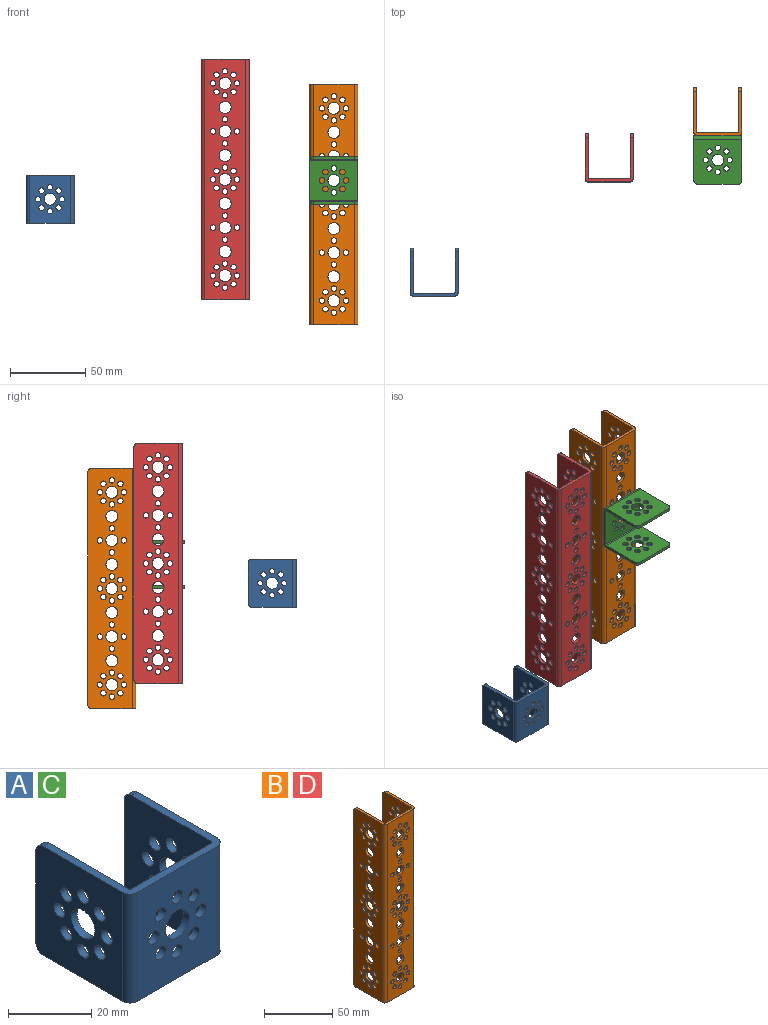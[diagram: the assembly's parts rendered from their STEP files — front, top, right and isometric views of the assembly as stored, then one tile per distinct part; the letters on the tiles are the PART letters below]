
ASSEMBLY  parts=4 mates=1
PART A: 45 faces, bbox 32x32x32 mm
  f0: cylinder r=2.5mm len=32mm, axis (0,0,-1), area 125.7mm2, adj f1,f11,f12,f13
  f1: plane 32x27mm, normal (0,-1,0), area 727.7mm2, adj f0,f2,f12,f13,f18,f23,f24,f25
  f2: cylinder r=2.5mm len=32mm, axis (0,0,-1), area 125.7mm2, adj f1,f3,f12,f13
  f3: plane 32x29.5mm, normal (1,0,0), area 805mm2, adj f2,f4,f12,f13,f14,f16,f20,f22
  f4: plane 27x2mm, normal (0,1,0), area 54mm2, adj f3,f5,f14,f16
  f5: plane 32x29.5mm, normal (-1,0,0), area 805mm2, adj f4,f6,f12,f13,f14,f16,f20,f22
  f6: cylinder r=0.5mm len=32mm, axis (0,0,-1), area 25.1mm2, adj f5,f7,f12,f13
  f7: plane 32x27mm, normal (0,1,0), area 727.7mm2, adj f6,f8,f12,f13,f18,f23,f24,f25
  f8: cylinder r=0.5mm len=32mm, axis (0,0,-1), area 25.1mm2, adj f7,f9,f12,f13
  f9: plane 32x29.5mm, normal (1,0,0), area 805mm2, adj f8,f10,f12,f13,f15,f17,f19,f21
  f10: plane 27x2mm, normal (0,1,0), area 54mm2, adj f9,f11,f15,f17
  f11: plane 32x29.5mm, normal (-1,0,0), area 805mm2, adj f0,f10,f12,f13,f15,f17,f19,f21
  f12: plane 32x29.5mm, normal (0,0,1), area 171.4mm2, adj f0,f1,f2,f3,f5,f6,f7,f8
  f13: plane 32x29.5mm, normal (0,0,-1), area 171.4mm2, adj f0,f1,f2,f3,f5,f6,f7,f8
  f14: cylinder r=2.5mm len=2.5mm, axis (-1,0,0), area 7.9mm2, adj f3,f4,f5,f13
  f15: cylinder r=2.5mm len=2.5mm, axis (-1,0,0), area 7.9mm2, adj f9,f10,f11,f13
  f16: cylinder r=2.5mm len=2.5mm, axis (1,0,0), area 7.9mm2, adj f3,f4,f5,f12
  f17: cylinder r=2.5mm len=2.5mm, axis (1,0,0), area 7.9mm2, adj f9,f10,f11,f12
  f18: cylinder r=4mm len=8mm, axis (0,-1,0), area 50.3mm2, adj f1,f7
  f19: cylinder r=4mm len=8mm, axis (-1,0,0), area 50.3mm2, adj f9,f11
  f20: cylinder r=4mm len=8mm, axis (-1,0,0), area 50.3mm2, adj f3,f5
  f21: cylinder r=1.85mm len=3.7mm, axis (-1,0,0), area 23.2mm2, adj f9,f11
  f22: cylinder r=1.85mm len=3.7mm, axis (-1,0,0), area 23.2mm2, adj f3,f5
  f23: cylinder r=1.85mm len=3.7mm, axis (0,-1,0), area 23.2mm2, adj f1,f7
  f24: cylinder r=1.85mm len=3.7mm, axis (0,-1,0), area 23.2mm2, adj f1,f7
  f25: cylinder r=1.85mm len=3.7mm, axis (0,-1,0), area 23.2mm2, adj f1,f7
  f26: cylinder r=1.85mm len=3.7mm, axis (0,-1,0), area 23.2mm2, adj f1,f7
  f27: cylinder r=1.85mm len=3.7mm, axis (0,-1,0), area 23.2mm2, adj f1,f7
  f28: cylinder r=1.85mm len=3.7mm, axis (0,-1,0), area 23.2mm2, adj f1,f7
  f29: cylinder r=1.85mm len=3.7mm, axis (0,-1,0), area 23.2mm2, adj f1,f7
  f30: cylinder r=1.85mm len=3.7mm, axis (0,-1,0), area 23.2mm2, adj f1,f7
  f31: cylinder r=1.85mm len=3.7mm, axis (-1,0,0), area 23.2mm2, adj f9,f11
  f32: cylinder r=1.85mm len=3.7mm, axis (-1,0,0), area 23.2mm2, adj f3,f5
  f33: cylinder r=1.85mm len=3.7mm, axis (-1,0,0), area 23.2mm2, adj f9,f11
  f34: cylinder r=1.85mm len=3.7mm, axis (-1,0,0), area 23.2mm2, adj f3,f5
  f35: cylinder r=1.85mm len=3.7mm, axis (-1,0,0), area 23.2mm2, adj f9,f11
  f36: cylinder r=1.85mm len=3.7mm, axis (-1,0,0), area 23.2mm2, adj f3,f5
  f37: cylinder r=1.85mm len=3.7mm, axis (-1,0,0), area 23.2mm2, adj f9,f11
  f38: cylinder r=1.85mm len=3.7mm, axis (-1,0,0), area 23.2mm2, adj f3,f5
  f39: cylinder r=1.85mm len=3.7mm, axis (-1,0,0), area 23.2mm2, adj f9,f11
  f40: cylinder r=1.85mm len=3.7mm, axis (-1,0,0), area 23.2mm2, adj f3,f5
  f41: cylinder r=1.85mm len=3.7mm, axis (-1,0,0), area 23.2mm2, adj f9,f11
  f42: cylinder r=1.85mm len=3.7mm, axis (-1,0,0), area 23.2mm2, adj f3,f5
  f43: cylinder r=1.85mm len=3.7mm, axis (-1,0,0), area 23.2mm2, adj f9,f11
  f44: cylinder r=1.85mm len=3.7mm, axis (-1,0,0), area 23.2mm2, adj f3,f5
PART B: 141 faces, bbox 32x32x160 mm
  f0: cylinder r=2.5mm len=160mm, axis (0,0,-1), area 628.3mm2, adj f1,f11,f12,f13
  f1: plane 160x27mm, normal (0,-1,0), area 3523.5mm2, adj f0,f2,f12,f13,f18,f23,f24,f25
  f2: cylinder r=2.5mm len=160mm, axis (0,0,-1), area 628.3mm2, adj f1,f3,f12,f13
  f3: plane 160x29.5mm, normal (1,0,0), area 3920.9mm2, adj f2,f4,f12,f13,f14,f17,f20,f22
  f4: plane 155x2mm, normal (0,1,0), area 310mm2, adj f3,f5,f14,f17
  f5: plane 160x29.5mm, normal (-1,0,0), area 3920.9mm2, adj f4,f6,f12,f13,f14,f17,f20,f22
  f6: cylinder r=0.5mm len=160mm, axis (0,0,-1), area 125.7mm2, adj f5,f7,f12,f13
  f7: plane 160x27mm, normal (0,1,0), area 3523.5mm2, adj f6,f8,f12,f13,f18,f23,f24,f25
  f8: cylinder r=0.5mm len=160mm, axis (0,0,-1), area 125.7mm2, adj f7,f9,f12,f13
  f9: plane 160x29.5mm, normal (1,0,0), area 3920.9mm2, adj f8,f10,f12,f13,f15,f16,f19,f21
  f10: plane 155x2mm, normal (0,1,0), area 310mm2, adj f9,f11,f15,f16
  f11: plane 160x29.5mm, normal (-1,0,0), area 3920.9mm2, adj f0,f10,f12,f13,f15,f16,f19,f21
  f12: plane 32x29.5mm, normal (0,0,1), area 171.4mm2, adj f0,f1,f2,f3,f5,f6,f7,f8
  f13: plane 32x29.5mm, normal (0,0,-1), area 171.4mm2, adj f0,f1,f2,f3,f5,f6,f7,f8
  f14: cylinder r=2.5mm len=2.5mm, axis (1,0,0), area 7.9mm2, adj f3,f4,f5,f12
  f15: cylinder r=2.5mm len=2.5mm, axis (1,0,0), area 7.9mm2, adj f9,f10,f11,f12
  f16: cylinder r=2.5mm len=2.5mm, axis (-1,0,0), area 7.9mm2, adj f9,f10,f11,f13
  f17: cylinder r=2.5mm len=2.5mm, axis (-1,0,0), area 7.9mm2, adj f3,f4,f5,f13
  f18: cylinder r=4mm len=8mm, axis (0,-1,0), area 50.3mm2, adj f1,f7
  f19: cylinder r=4mm len=8mm, axis (-1,0,0), area 50.3mm2, adj f9,f11
  f20: cylinder r=4mm len=8mm, axis (-1,0,0), area 50.3mm2, adj f3,f5
  f21: cylinder r=1.85mm len=3.7mm, axis (-1,0,0), area 23.2mm2, adj f9,f11
  f22: cylinder r=1.85mm len=3.7mm, axis (-1,0,0), area 23.2mm2, adj f3,f5
  f23: cylinder r=1.85mm len=3.7mm, axis (0,-1,0), area 23.2mm2, adj f1,f7
  f24: cylinder r=4mm len=8mm, axis (0,-1,0), area 50.3mm2, adj f1,f7
  f25: cylinder r=4mm len=8mm, axis (0,-1,0), area 50.3mm2, adj f1,f7
  f26: cylinder r=4mm len=8mm, axis (0,-1,0), area 50.3mm2, adj f1,f7
  f27: cylinder r=4mm len=8mm, axis (0,-1,0), area 50.3mm2, adj f1,f7
  f28: cylinder r=4mm len=8mm, axis (0,-1,0), area 50.3mm2, adj f1,f7
  f29: cylinder r=4mm len=8mm, axis (0,-1,0), area 50.3mm2, adj f1,f7
  f30: cylinder r=4mm len=8mm, axis (0,-1,0), area 50.3mm2, adj f1,f7
  f31: cylinder r=4mm len=8mm, axis (0,-1,0), area 50.3mm2, adj f1,f7
  f32: cylinder r=4mm len=8mm, axis (-1,0,0), area 50.3mm2, adj f9,f11
  f33: cylinder r=4mm len=8mm, axis (-1,0,0), area 50.3mm2, adj f3,f5
  f34: cylinder r=4mm len=8mm, axis (-1,0,0), area 50.3mm2, adj f9,f11
  f35: cylinder r=4mm len=8mm, axis (-1,0,0), area 50.3mm2, adj f3,f5
  f36: cylinder r=4mm len=8mm, axis (-1,0,0), area 50.3mm2, adj f9,f11
  f37: cylinder r=4mm len=8mm, axis (-1,0,0), area 50.3mm2, adj f3,f5
  f38: cylinder r=4mm len=8mm, axis (-1,0,0), area 50.3mm2, adj f9,f11
  f39: cylinder r=4mm len=8mm, axis (-1,0,0), area 50.3mm2, adj f3,f5
  f40: cylinder r=4mm len=8mm, axis (-1,0,0), area 50.3mm2, adj f9,f11
  f41: cylinder r=4mm len=8mm, axis (-1,0,0), area 50.3mm2, adj f3,f5
  f42: cylinder r=4mm len=8mm, axis (-1,0,0), area 50.3mm2, adj f9,f11
  f43: cylinder r=4mm len=8mm, axis (-1,0,0), area 50.3mm2, adj f3,f5
  f44: cylinder r=4mm len=8mm, axis (-1,0,0), area 50.3mm2, adj f9,f11
  f45: cylinder r=4mm len=8mm, axis (-1,0,0), area 50.3mm2, adj f3,f5
  f46: cylinder r=4mm len=8mm, axis (-1,0,0), area 50.3mm2, adj f9,f11
  f47: cylinder r=4mm len=8mm, axis (-1,0,0), area 50.3mm2, adj f3,f5
  f48: cylinder r=1.85mm len=3.7mm, axis (0,-1,0), area 23.2mm2, adj f1,f7
  f49: cylinder r=1.85mm len=3.7mm, axis (0,-1,0), area 23.2mm2, adj f1,f7
  f50: cylinder r=1.85mm len=3.7mm, axis (0,-1,0), area 23.2mm2, adj f1,f7
  f51: cylinder r=1.85mm len=3.7mm, axis (0,-1,0), area 23.2mm2, adj f1,f7
  f52: cylinder r=1.85mm len=3.7mm, axis (0,-1,0), area 23.2mm2, adj f1,f7
  f53: cylinder r=1.85mm len=3.7mm, axis (0,-1,0), area 23.2mm2, adj f1,f7
  f54: cylinder r=1.85mm len=3.7mm, axis (0,-1,0), area 23.2mm2, adj f1,f7
  f55: cylinder r=1.85mm len=3.7mm, axis (-1,0,0), area 23.2mm2, adj f9,f11
  f56: cylinder r=1.85mm len=3.7mm, axis (-1,0,0), area 23.2mm2, adj f3,f5
  f57: cylinder r=1.85mm len=3.7mm, axis (-1,0,0), area 23.2mm2, adj f9,f11
  f58: cylinder r=1.85mm len=3.7mm, axis (-1,0,0), area 23.2mm2, adj f3,f5
  f59: cylinder r=1.85mm len=3.7mm, axis (-1,0,0), area 23.2mm2, adj f9,f11
  f60: cylinder r=1.85mm len=3.7mm, axis (-1,0,0), area 23.2mm2, adj f3,f5
  f61: cylinder r=1.85mm len=3.7mm, axis (-1,0,0), area 23.2mm2, adj f9,f11
  f62: cylinder r=1.85mm len=3.7mm, axis (-1,0,0), area 23.2mm2, adj f3,f5
  f63: cylinder r=1.85mm len=3.7mm, axis (-1,0,0), area 23.2mm2, adj f9,f11
  f64: cylinder r=1.85mm len=3.7mm, axis (-1,0,0), area 23.2mm2, adj f3,f5
  f65: cylinder r=1.85mm len=3.7mm, axis (-1,0,0), area 23.2mm2, adj f9,f11
  f66: cylinder r=1.85mm len=3.7mm, axis (-1,0,0), area 23.2mm2, adj f3,f5
  f67: cylinder r=1.85mm len=3.7mm, axis (-1,0,0), area 23.2mm2, adj f9,f11
  f68: cylinder r=1.85mm len=3.7mm, axis (-1,0,0), area 23.2mm2, adj f3,f5
  f69: cylinder r=1.85mm len=3.7mm, axis (0,-1,0), area 23.2mm2, adj f1,f7
  f70: cylinder r=1.85mm len=3.7mm, axis (-1,0,0), area 23.2mm2, adj f9,f11
  f71: cylinder r=1.85mm len=3.7mm, axis (-1,0,0), area 23.2mm2, adj f3,f5
  f72: cylinder r=1.85mm len=3.7mm, axis (0,-1,0), area 23.2mm2, adj f1,f7
  f73: cylinder r=1.85mm len=3.7mm, axis (0,-1,0), area 23.2mm2, adj f1,f7
  f74: cylinder r=1.85mm len=3.7mm, axis (0,-1,0), area 23.2mm2, adj f1,f7
  f75: cylinder r=1.85mm len=3.7mm, axis (-1,0,0), area 23.2mm2, adj f9,f11
  f76: cylinder r=1.85mm len=3.7mm, axis (-1,0,0), area 23.2mm2, adj f3,f5
  f77: cylinder r=1.85mm len=3.7mm, axis (-1,0,0), area 23.2mm2, adj f9,f11
  f78: cylinder r=1.85mm len=3.7mm, axis (-1,0,0), area 23.2mm2, adj f3,f5
  f79: cylinder r=1.85mm len=3.7mm, axis (-1,0,0), area 23.2mm2, adj f9,f11
  f80: cylinder r=1.85mm len=3.7mm, axis (-1,0,0), area 23.2mm2, adj f3,f5
  f81: cylinder r=1.85mm len=3.7mm, axis (0,-1,0), area 23.2mm2, adj f1,f7
  f82: cylinder r=1.85mm len=3.7mm, axis (0,-1,0), area 23.2mm2, adj f1,f7
  f83: cylinder r=1.85mm len=3.7mm, axis (0,-1,0), area 23.2mm2, adj f1,f7
  f84: cylinder r=1.85mm len=3.7mm, axis (0,-1,0), area 23.2mm2, adj f1,f7
  f85: cylinder r=1.85mm len=3.7mm, axis (0,-1,0), area 23.2mm2, adj f1,f7
  f86: cylinder r=1.85mm len=3.7mm, axis (0,-1,0), area 23.2mm2, adj f1,f7
  f87: cylinder r=1.85mm len=3.7mm, axis (0,-1,0), area 23.2mm2, adj f1,f7
  f88: cylinder r=1.85mm len=3.7mm, axis (0,-1,0), area 23.2mm2, adj f1,f7
  f89: cylinder r=1.85mm len=3.7mm, axis (-1,0,0), area 23.2mm2, adj f9,f11
  f90: cylinder r=1.85mm len=3.7mm, axis (-1,0,0), area 23.2mm2, adj f3,f5
  f91: cylinder r=1.85mm len=3.7mm, axis (-1,0,0), area 23.2mm2, adj f9,f11
  f92: cylinder r=1.85mm len=3.7mm, axis (-1,0,0), area 23.2mm2, adj f3,f5
  f93: cylinder r=1.85mm len=3.7mm, axis (-1,0,0), area 23.2mm2, adj f9,f11
  f94: cylinder r=1.85mm len=3.7mm, axis (-1,0,0), area 23.2mm2, adj f3,f5
  f95: cylinder r=1.85mm len=3.7mm, axis (-1,0,0), area 23.2mm2, adj f9,f11
  f96: cylinder r=1.85mm len=3.7mm, axis (-1,0,0), area 23.2mm2, adj f3,f5
  f97: cylinder r=1.85mm len=3.7mm, axis (-1,0,0), area 23.2mm2, adj f9,f11
  f98: cylinder r=1.85mm len=3.7mm, axis (-1,0,0), area 23.2mm2, adj f3,f5
  f99: cylinder r=1.85mm len=3.7mm, axis (-1,0,0), area 23.2mm2, adj f9,f11
  f100: cylinder r=1.85mm len=3.7mm, axis (-1,0,0), area 23.2mm2, adj f3,f5
  f101: cylinder r=1.85mm len=3.7mm, axis (-1,0,0), area 23.2mm2, adj f9,f11
  f102: cylinder r=1.85mm len=3.7mm, axis (-1,0,0), area 23.2mm2, adj f3,f5
  f103: cylinder r=1.85mm len=3.7mm, axis (-1,0,0), area 23.2mm2, adj f9,f11
  f104: cylinder r=1.85mm len=3.7mm, axis (-1,0,0), area 23.2mm2, adj f3,f5
  f105: cylinder r=1.85mm len=3.7mm, axis (0,-1,0), area 23.2mm2, adj f1,f7
  f106: cylinder r=1.85mm len=3.7mm, axis (0,-1,0), area 23.2mm2, adj f1,f7
  f107: cylinder r=1.85mm len=3.7mm, axis (0,-1,0), area 23.2mm2, adj f1,f7
  f108: cylinder r=1.85mm len=3.7mm, axis (0,-1,0), area 23.2mm2, adj f1,f7
  f109: cylinder r=1.85mm len=3.7mm, axis (-1,0,0), area 23.2mm2, adj f3,f5
  f110: cylinder r=1.85mm len=3.7mm, axis (-1,0,0), area 23.2mm2, adj f3,f5
  f111: cylinder r=1.85mm len=3.7mm, axis (-1,0,0), area 23.2mm2, adj f3,f5
  f112: cylinder r=1.85mm len=3.7mm, axis (-1,0,0), area 23.2mm2, adj f3,f5
  f113: cylinder r=1.85mm len=3.7mm, axis (-1,0,0), area 23.2mm2, adj f9,f11
  f114: cylinder r=1.85mm len=3.7mm, axis (-1,0,0), area 23.2mm2, adj f9,f11
  f115: cylinder r=1.85mm len=3.7mm, axis (-1,0,0), area 23.2mm2, adj f9,f11
  f116: cylinder r=1.85mm len=3.7mm, axis (-1,0,0), area 23.2mm2, adj f9,f11
  f117: cylinder r=1.85mm len=3.7mm, axis (-1,0,0), area 23.2mm2, adj f3,f5
  f118: cylinder r=1.85mm len=3.7mm, axis (-1,0,0), area 23.2mm2, adj f3,f5
  f119: cylinder r=1.85mm len=3.7mm, axis (-1,0,0), area 23.2mm2, adj f3,f5
  f120: cylinder r=1.85mm len=3.7mm, axis (-1,0,0), area 23.2mm2, adj f3,f5
  f121: cylinder r=1.85mm len=3.7mm, axis (-1,0,0), area 23.2mm2, adj f3,f5
  f122: cylinder r=1.85mm len=3.7mm, axis (-1,0,0), area 23.2mm2, adj f3,f5
  f123: cylinder r=1.85mm len=3.7mm, axis (-1,0,0), area 23.2mm2, adj f3,f5
  f124: cylinder r=1.85mm len=3.7mm, axis (-1,0,0), area 23.2mm2, adj f3,f5
  f125: cylinder r=1.85mm len=3.7mm, axis (-1,0,0), area 23.2mm2, adj f9,f11
  f126: cylinder r=1.85mm len=3.7mm, axis (-1,0,0), area 23.2mm2, adj f9,f11
  f127: cylinder r=1.85mm len=3.7mm, axis (-1,0,0), area 23.2mm2, adj f9,f11
  f128: cylinder r=1.85mm len=3.7mm, axis (-1,0,0), area 23.2mm2, adj f9,f11
  f129: cylinder r=1.85mm len=3.7mm, axis (-1,0,0), area 23.2mm2, adj f9,f11
  f130: cylinder r=1.85mm len=3.7mm, axis (-1,0,0), area 23.2mm2, adj f9,f11
  f131: cylinder r=1.85mm len=3.7mm, axis (-1,0,0), area 23.2mm2, adj f9,f11
  f132: cylinder r=1.85mm len=3.7mm, axis (-1,0,0), area 23.2mm2, adj f9,f11
  f133: cylinder r=1.85mm len=3.7mm, axis (0,-1,0), area 23.2mm2, adj f1,f7
  f134: cylinder r=1.85mm len=3.7mm, axis (0,-1,0), area 23.2mm2, adj f1,f7
  f135: cylinder r=1.85mm len=3.7mm, axis (0,-1,0), area 23.2mm2, adj f1,f7
  f136: cylinder r=1.85mm len=3.7mm, axis (0,-1,0), area 23.2mm2, adj f1,f7
  f137: cylinder r=1.85mm len=3.7mm, axis (0,-1,0), area 23.2mm2, adj f1,f7
  f138: cylinder r=1.85mm len=3.7mm, axis (0,-1,0), area 23.2mm2, adj f1,f7
  f139: cylinder r=1.85mm len=3.7mm, axis (0,-1,0), area 23.2mm2, adj f1,f7
  f140: cylinder r=1.85mm len=3.7mm, axis (0,-1,0), area 23.2mm2, adj f1,f7
PART C: same geometry as A
PART D: same geometry as B
PLACE A t=(-168.39,-94.12,28.65)mm
PLACE B t=(20.37,12.47,25.07)mm fixed
PLACE C rot(axis=(0.71,0,-0.71),180deg) t=(20.37,12.47,41.07)mm
PLACE D t=(-52,-18.22,41.71)mm
MATE fastened C.f18 <-> B.f24  axis (0,1,0) through (20.37,12.47,41.07)mm
